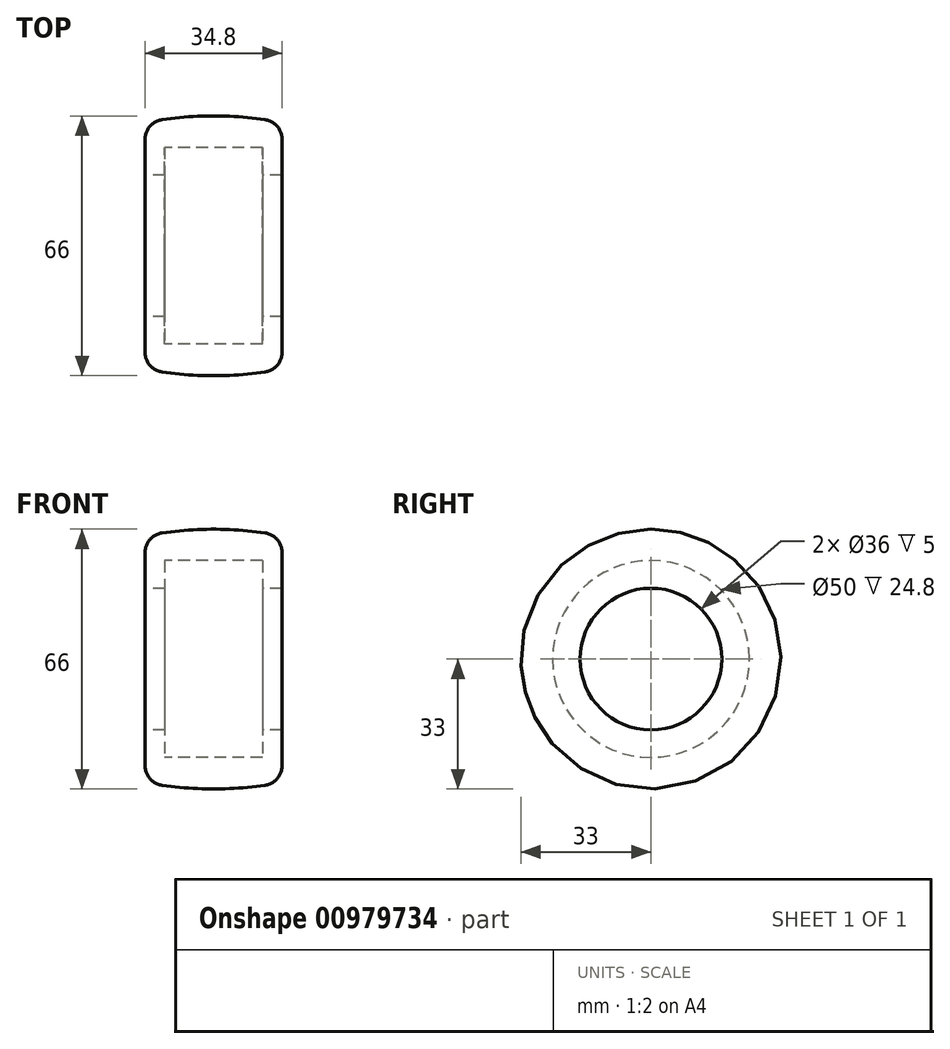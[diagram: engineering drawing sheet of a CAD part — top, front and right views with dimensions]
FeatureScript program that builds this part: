
annotation { "Feature Type Name" : "Feature", "Feature Type Description" : "" }
export const myFeature = defineFeature(function(context is Context, id is Id, definition is map)
    precondition{}
    {
        {
            var Q0;
            Q0=qCreatedBy(makeId("Front.planeOp"),FACE);
            var sketch = newSketch(context, id + "F0", { "sketchPlane" : qUnion([Q0])});
            skLineSegment(sketch, "E0.left", {"start": v(-17.4, 18) * mm, "end": v(-17.4, 27.1) * mm});
            skPoint(sketch, "E1.center.orphan", {"position": v(0, -57) * mm});
            skPoint(sketch, "E2.start.orphan", {"position": v(-44.08, 0) * mm});
            skArc(sketch, "E3", {"start": v(13.13, 32.04) * mm, "mid": v(0, 33) * mm, "end": v(-13.13, 32.04) * mm});
            skLineSegment(sketch, "E4", {"start": v(17.4, 27.1) * mm, "end": v(17.4, 18) * mm});
            skArc(sketch, "E5", {"start": v(-13.13, 32.04) * mm, "mid": v(-16.18, 30.36) * mm, "end": v(-17.4, 27.1) * mm});
            skArc(sketch, "E6", {"start": v(17.4, 27.1) * mm, "mid": v(16.18, 30.36) * mm, "end": v(13.13, 32.04) * mm});
            skLineSegment(sketch, "E7", {"start": v(-44.08, 0) * mm, "end": v(-17.4, 0) * mm, "construction": true});
            skLineSegment(sketch, "E8.bottom", {"start": v(12.4, 25) * mm, "end": v(-12.4, 25) * mm});
            skLineSegment(sketch, "E8.left", {"start": v(12.4, 25) * mm, "end": v(12.4, 18) * mm});
            skLineSegment(sketch, "E8.right", {"start": v(-12.4, 25) * mm, "end": v(-12.4, 18) * mm});
            skPoint(sketch, "E8.middle", {"position": v(0, 0) * mm});
            skLineSegment(sketch, "E9", {"start": v(-17.4, 18) * mm, "end": v(-12.4, 18) * mm});
            skPoint(sketch, "E8.top.end.orphan", {"position": v(-12.4, -25) * mm});
            skPoint(sketch, "E10.orphan", {"position": v(12.4, -25) * mm});
            skLineSegment(sketch, "E11.trimOffspring", {"start": v(17.4, 0) * mm, "end": v(42.56, 0) * mm, "construction": true});
            skLineSegment(sketch, "E12.trimOffspring", {"start": v(12.4, 18) * mm, "end": v(17.4, 18) * mm});
            skSolve(sketch);
        }
        {
            var Q0;
            Q0 = qSketchRegion(id + "F0", true);
            var Q1;
            Q1=sQuery(id+"F0.wireOp",EDGE,"E7");
            revolve(context, id + "F1", {"surfaceOperationType" : NewSurfaceOperationType.NEW, "entities" : qUnion([Q0]), "axis" : qUnion([Q1]), "revolveType" : RevolveType.FULL});
        }
    });
